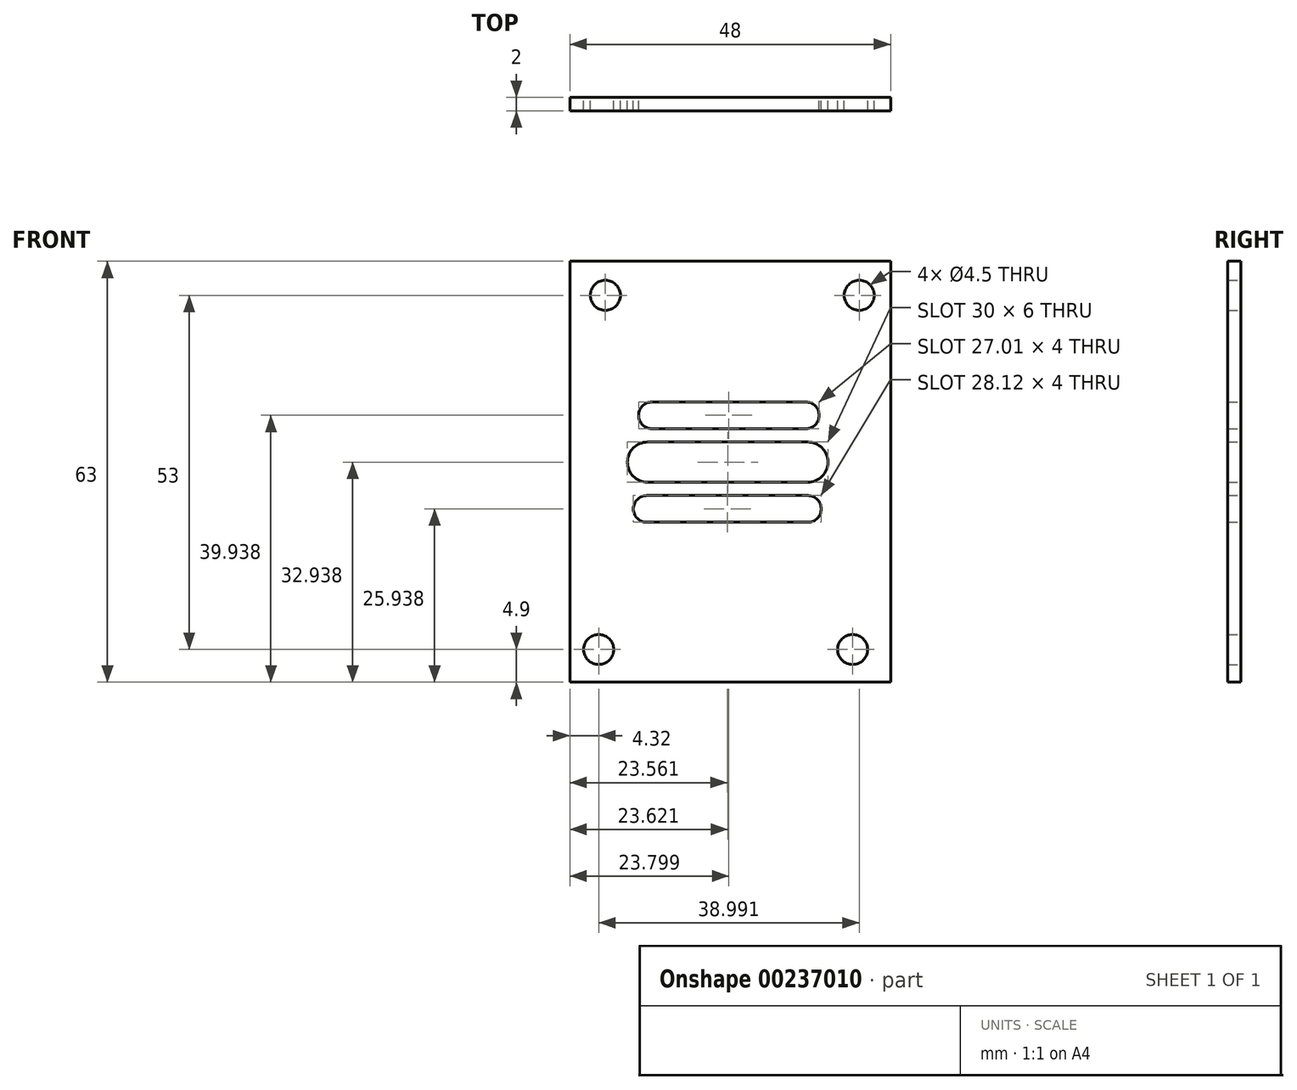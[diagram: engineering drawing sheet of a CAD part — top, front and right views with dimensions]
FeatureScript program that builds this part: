
annotation { "Feature Type Name" : "Feature", "Feature Type Description" : "" }
export const myFeature = defineFeature(function(context is Context, id is Id, definition is map)
    precondition{}
    {
        {
            var Q0;
            Q0=qCreatedBy(makeId("Front.planeOp"),FACE);
            var sketch = newSketch(context, id + "F0", { "sketchPlane" : qUnion([Q0])});
            skLineSegment(sketch, "E0", {"start": v(0, 0) * mm, "end": v(0, 63) * mm});
            skLineSegment(sketch, "E1", {"start": v(0, 63) * mm, "end": v(48, 63) * mm});
            skLineSegment(sketch, "E2", {"start": v(48, 63) * mm, "end": v(48, 0) * mm});
            skLineSegment(sketch, "E3", {"start": v(48, 0) * mm, "end": v(0, 0) * mm});
            skCircle(sketch, "E4", {"center": v(5.31, 57.9) * mm, "radius": 2.25 * mm});
            skCircle(sketch, "E5", {"center": v(43.31, 57.9) * mm, "radius": 2.25 * mm});
            skCircle(sketch, "E6", {"center": v(4.32, 4.9) * mm, "radius": 2.25 * mm});
            skCircle(sketch, "E7", {"center": v(42.32, 4.9) * mm, "radius": 2.25 * mm});
            skLineSegment(sketch, "E8.bottom", {"start": v(11.62, 35.94) * mm, "end": v(35.62, 35.94) * mm});
            skLineSegment(sketch, "E8.top", {"start": v(11.62, 29.94) * mm, "end": v(35.62, 29.94) * mm});
            skArc(sketch, "E9", {"start": v(11.62, 35.94) * mm, "mid": v(8.62, 32.94) * mm, "end": v(11.62, 29.94) * mm});
            skArc(sketch, "E10", {"start": v(35.62, 29.94) * mm, "mid": v(38.62, 32.94) * mm, "end": v(35.62, 35.94) * mm});
            skLineSegment(sketch, "E11", {"start": v(11.62, 32.94) * mm, "end": v(35.62, 32.94) * mm, "construction": true});
            skLineSegment(sketch, "E12.bottom", {"start": v(12.3, 41.94) * mm, "end": v(35.3, 41.94) * mm});
            skLineSegment(sketch, "E12.top", {"start": v(12.3, 37.94) * mm, "end": v(35.3, 37.94) * mm});
            skLineSegment(sketch, "E13", {"start": v(12.3, 39.94) * mm, "end": v(35.3, 39.94) * mm, "construction": true});
            skArc(sketch, "E14", {"start": v(12.3, 41.94) * mm, "mid": v(10.3, 39.94) * mm, "end": v(12.3, 37.94) * mm});
            skArc(sketch, "E15", {"start": v(35.3, 37.94) * mm, "mid": v(37.3, 39.94) * mm, "end": v(35.3, 41.94) * mm});
            skLineSegment(sketch, "E16.bottom", {"start": v(11.5, 27.94) * mm, "end": v(35.62, 27.94) * mm});
            skLineSegment(sketch, "E16.top", {"start": v(11.5, 23.94) * mm, "end": v(35.62, 23.94) * mm});
            skArc(sketch, "E17", {"start": v(11.5, 27.94) * mm, "mid": v(9.5, 25.94) * mm, "end": v(11.5, 23.94) * mm});
            skArc(sketch, "E18", {"start": v(35.62, 23.94) * mm, "mid": v(37.62, 25.94) * mm, "end": v(35.62, 27.94) * mm});
            skLineSegment(sketch, "E19", {"start": v(11.5, 25.94) * mm, "end": v(35.62, 25.94) * mm, "construction": true});
            skSolve(sketch);
        }
        {
            var Q0;
            Q0=makeQuery(id+"F0.imprint","IMPRINT",FACE,{"disambiguationData":[TD([[makeQuery(id+"F0.imprint","IMPRINT",EDGE,{"derivedFrom":sQuery(id+"F0.wireOp",EDGE,"E0")}),-1.0]])]});
            extrude(context, id + "F1", {"entities" : qUnion([Q0]), "depth" : 2 * mm});
        }
    });
